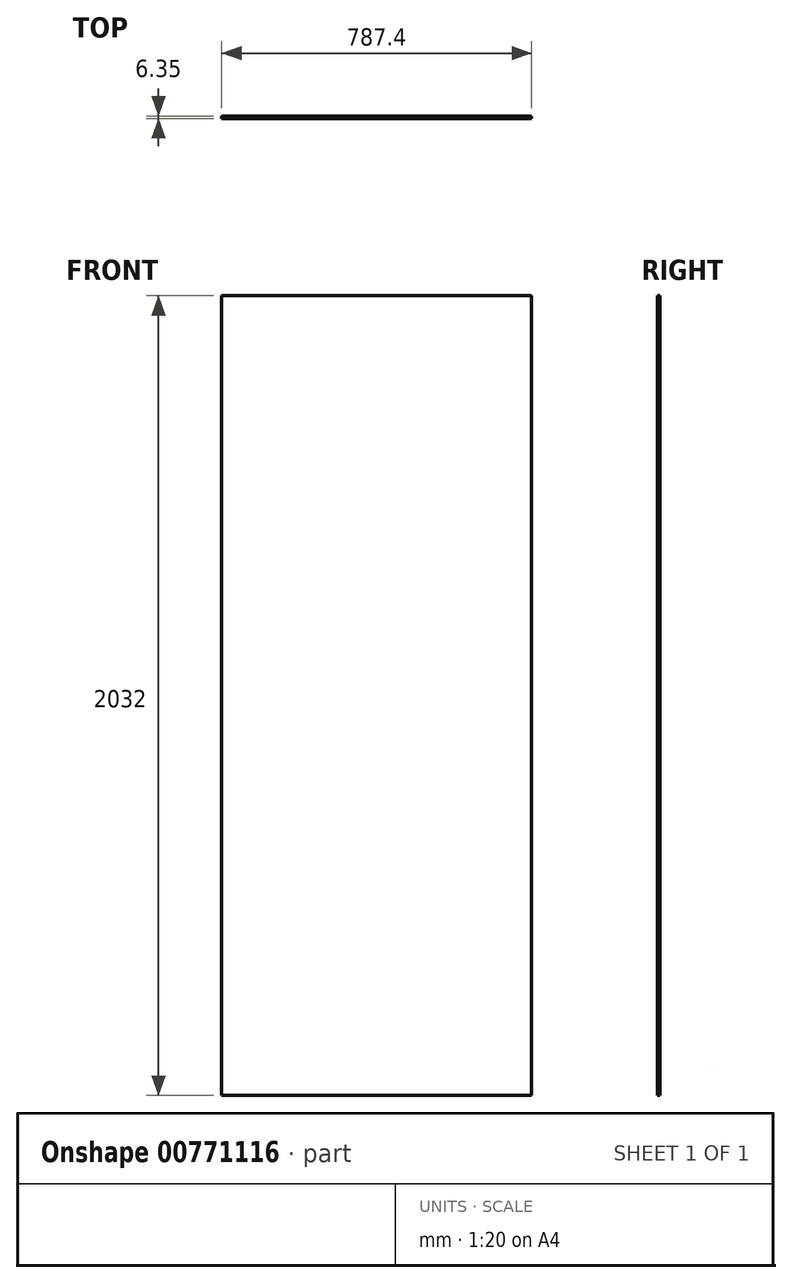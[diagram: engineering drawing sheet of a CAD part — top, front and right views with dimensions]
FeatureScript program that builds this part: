
annotation { "Feature Type Name" : "Feature", "Feature Type Description" : "" }
export const myFeature = defineFeature(function(context is Context, id is Id, definition is map)
    precondition{}
    {
        {
            var Q0;
            Q0=qCreatedBy(makeId("Front.planeOp"),FACE);
            var sketch = newSketch(context, id + "F0", { "sketchPlane" : qUnion([Q0])});
            skLineSegment(sketch, "E0.bottom", {"start": v(-787.4, 2032) * mm, "end": v(0, 2032) * mm});
            skLineSegment(sketch, "E0.top", {"start": v(-787.4, 0) * mm, "end": v(0, 0) * mm});
            skLineSegment(sketch, "E0.left", {"start": v(-787.4, 2032) * mm, "end": v(-787.4, 0) * mm});
            skLineSegment(sketch, "E0.right", {"start": v(0, 2032) * mm, "end": v(0, 0) * mm});
            skSolve(sketch);
        }
        {
            var Q0;
            Q0=makeQuery(id+"F0.imprint","IMPRINT",FACE,{"disambiguationData":[TD([[makeQuery(id+"F0.imprint","IMPRINT",EDGE,{"derivedFrom":sQuery(id+"F0.wireOp",EDGE,"E0.bottom")}),-1.0]])]});
            extrude(context, id + "F1", {"entities" : qUnion([Q0]), "depth" : 6.35 * mm, "offsetDistance" : 25.4 * mm});
        }
    });
